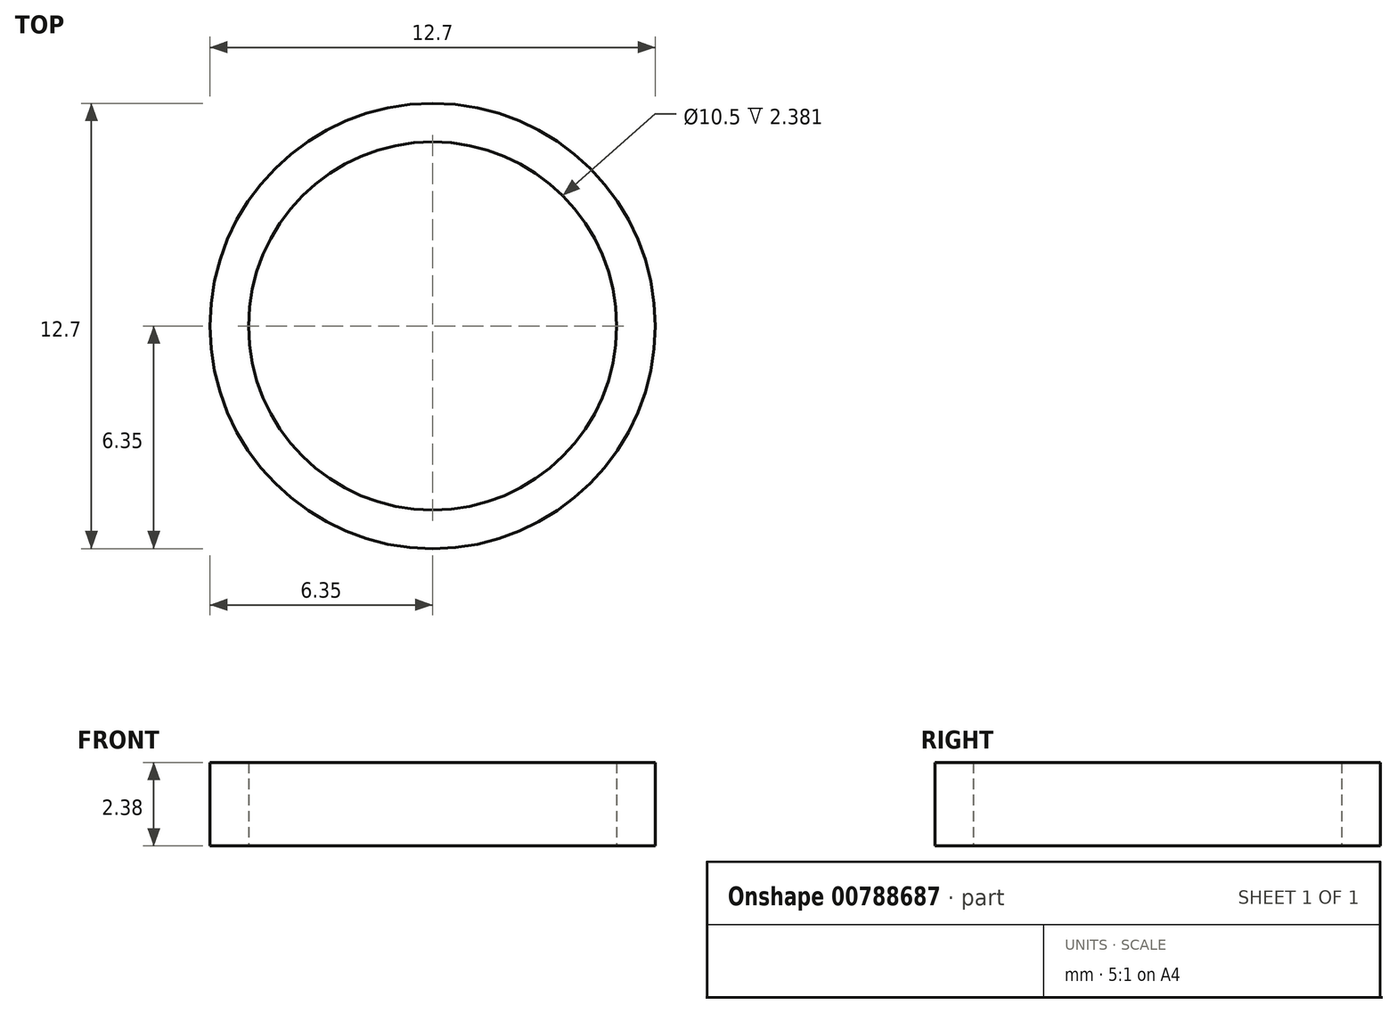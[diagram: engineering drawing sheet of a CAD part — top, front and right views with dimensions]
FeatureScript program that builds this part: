
annotation { "Feature Type Name" : "Feature", "Feature Type Description" : "" }
export const myFeature = defineFeature(function(context is Context, id is Id, definition is map)
    precondition{}
    {
        {
            var Q0;
            Q0=qCreatedBy(makeId("Top.planeOp"),FACE);
            var sketch = newSketch(context, id + "F0", { "sketchPlane" : qUnion([Q0])});
            skCircle(sketch, "E0", {"center": v(0, 0) * mm, "radius": 6.35 * mm});
            skCircle(sketch, "E1", {"center": v(0, 0) * mm, "radius": 5.25 * mm});
            skSolve(sketch);
        }
        {
            var Q0;
            Q0=makeQuery(id+"F0.imprint","IMPRINT",FACE,{"disambiguationData":[TD([[makeQuery(id+"F0.imprint","IMPRINT",EDGE,{"derivedFrom":sQuery(id+"F0.wireOp",EDGE,"E0")}),1.0]])]});
            extrude(context, id + "F1", {"entities" : qUnion([Q0]), "depth" : 2.38 * mm, "offsetDistance" : 25.4 * mm});
        }
    });
